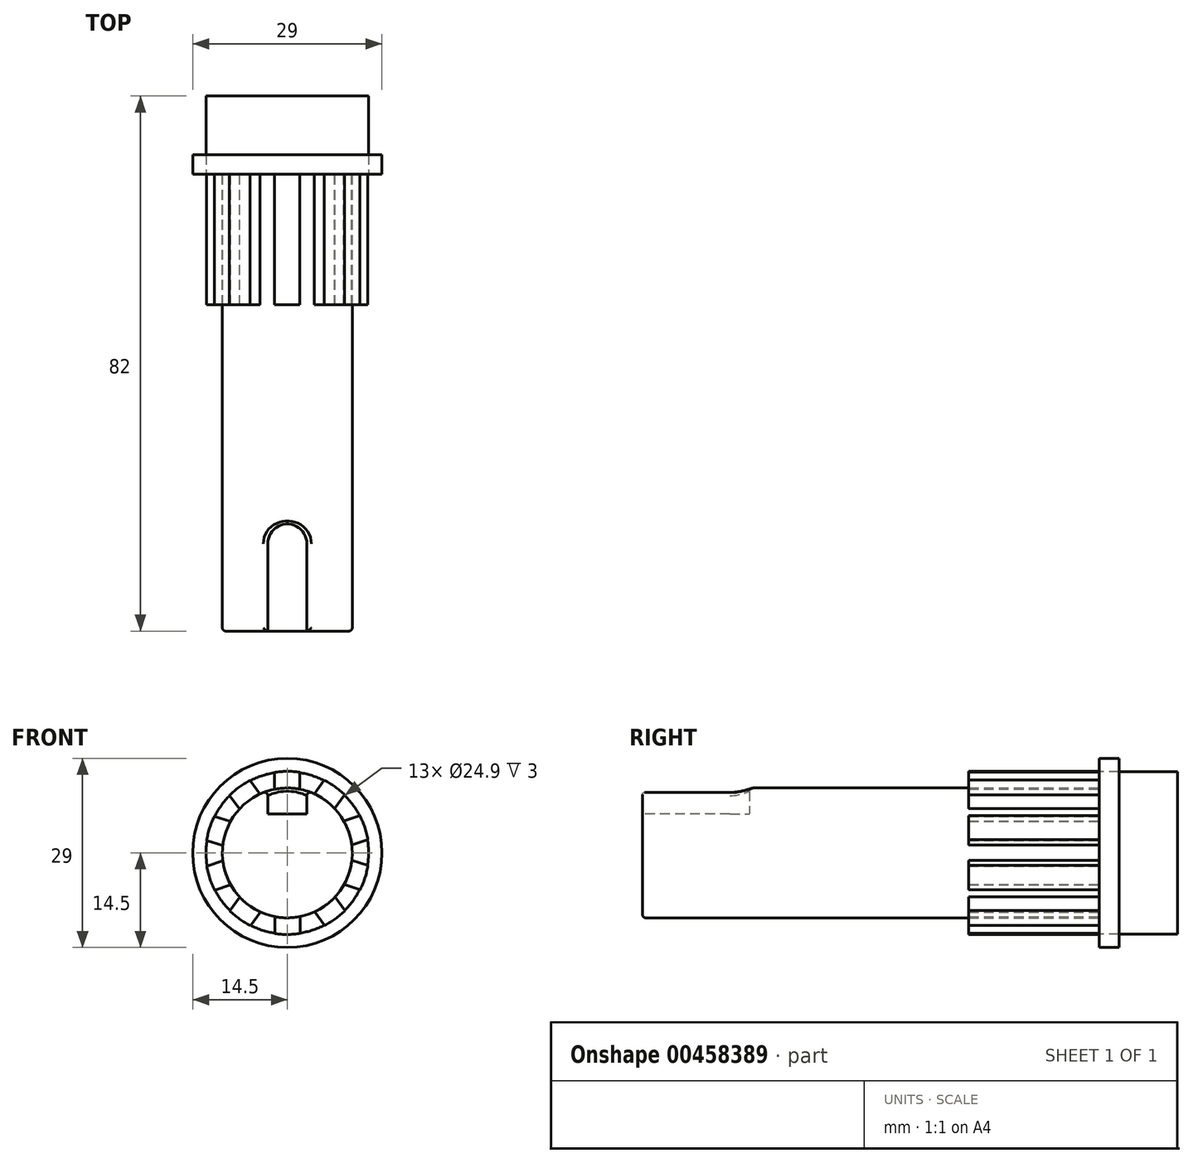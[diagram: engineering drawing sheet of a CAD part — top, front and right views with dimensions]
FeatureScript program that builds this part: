
annotation { "Feature Type Name" : "Feature", "Feature Type Description" : "" }
export const myFeature = defineFeature(function(context is Context, id is Id, definition is map)
    precondition{}
    {
        {
            var Q0;
            Q0=qCreatedBy(makeId("Front.planeOp"),FACE);
            var sketch = newSketch(context, id + "F0", { "sketchPlane" : qUnion([Q0])});
            skCircle(sketch, "E0", {"center": v(0, 0) * mm, "radius": 14.5 * mm});
            skCircle(sketch, "E1", {"center": v(0, 0) * mm, "radius": 9.95 * mm});
            skArc(sketch, "E2", {"start": v(-1.9, -12.36) * mm, "mid": v(0.05, -12.5) * mm, "end": v(1.99, -12.34) * mm});
            skLineSegment(sketch, "E3", {"start": v(-1.9, -12.36) * mm, "end": v(-1.9, -9.77) * mm});
            skLineSegment(sketch, "E4", {"start": v(1.97, -9.75) * mm, "end": v(1.99, -12.34) * mm});
            skLineSegment(sketch, "E5.1.0", {"start": v(7.32, -6.73) * mm, "end": v(8.86, -8.81) * mm});
            skLineSegment(sketch, "E5.1.2", {"start": v(5.73, -11.1) * mm, "end": v(4.2, -9.02) * mm});
            skArc(sketch, "E5.1.3", {"start": v(5.73, -11.1) * mm, "mid": v(7.39, -10.08) * mm, "end": v(8.86, -8.81) * mm});
            skLineSegment(sketch, "E5.2.0", {"start": v(9.88, -1.14) * mm, "end": v(12.35, -1.92) * mm});
            skLineSegment(sketch, "E5.2.2", {"start": v(11.17, -5.62) * mm, "end": v(8.7, -4.82) * mm});
            skArc(sketch, "E5.2.3", {"start": v(11.17, -5.62) * mm, "mid": v(11.9, -3.82) * mm, "end": v(12.35, -1.92) * mm});
            skLineSegment(sketch, "E5.3.0", {"start": v(8.67, 4.88) * mm, "end": v(11.12, 5.7) * mm});
            skLineSegment(sketch, "E5.3.2", {"start": v(12.34, 2.02) * mm, "end": v(9.88, 1.22) * mm});
            skArc(sketch, "E5.3.3", {"start": v(12.34, 2.02) * mm, "mid": v(11.87, 3.9) * mm, "end": v(11.12, 5.7) * mm});
            skLineSegment(sketch, "E5.4.0", {"start": v(4.14, 9.05) * mm, "end": v(5.64, 11.15) * mm});
            skLineSegment(sketch, "E5.4.2", {"start": v(8.8, 8.88) * mm, "end": v(7.27, 6.79) * mm});
            skArc(sketch, "E5.4.3", {"start": v(8.8, 8.88) * mm, "mid": v(7.3, 10.14) * mm, "end": v(5.64, 11.15) * mm});
            skLineSegment(sketch, "E5.5.0", {"start": v(-1.97, 9.75) * mm, "end": v(-1.99, 12.34) * mm});
            skLineSegment(sketch, "E5.5.2", {"start": v(1.9, 12.36) * mm, "end": v(1.9, 9.77) * mm});
            skArc(sketch, "E5.5.3", {"start": v(1.9, 12.36) * mm, "mid": v(-0.05, 12.5) * mm, "end": v(-1.99, 12.34) * mm});
            skLineSegment(sketch, "E5.6.0", {"start": v(-7.32, 6.73) * mm, "end": v(-8.86, 8.81) * mm});
            skLineSegment(sketch, "E5.6.2", {"start": v(-5.73, 11.1) * mm, "end": v(-4.2, 9.02) * mm});
            skArc(sketch, "E5.6.3", {"start": v(-5.73, 11.1) * mm, "mid": v(-7.39, 10.08) * mm, "end": v(-8.86, 8.81) * mm});
            skLineSegment(sketch, "E5.7.0", {"start": v(-9.88, 1.14) * mm, "end": v(-12.35, 1.92) * mm});
            skLineSegment(sketch, "E5.7.2", {"start": v(-11.17, 5.62) * mm, "end": v(-8.7, 4.82) * mm});
            skArc(sketch, "E5.7.3", {"start": v(-11.17, 5.62) * mm, "mid": v(-11.9, 3.82) * mm, "end": v(-12.35, 1.92) * mm});
            skLineSegment(sketch, "E5.8.0", {"start": v(-8.67, -4.88) * mm, "end": v(-11.12, -5.7) * mm});
            skLineSegment(sketch, "E5.8.2", {"start": v(-12.34, -2.02) * mm, "end": v(-9.88, -1.22) * mm});
            skArc(sketch, "E5.8.3", {"start": v(-12.34, -2.02) * mm, "mid": v(-11.87, -3.9) * mm, "end": v(-11.12, -5.7) * mm});
            skLineSegment(sketch, "E5.9.0", {"start": v(-4.14, -9.05) * mm, "end": v(-5.64, -11.15) * mm});
            skLineSegment(sketch, "E5.9.2", {"start": v(-8.8, -8.88) * mm, "end": v(-7.27, -6.79) * mm});
            skArc(sketch, "E5.9.3", {"start": v(-8.8, -8.88) * mm, "mid": v(-7.3, -10.14) * mm, "end": v(-5.64, -11.15) * mm});
            skSolve(sketch);
        }
        {
            var Q0;
            Q0=qCreatedBy(makeId("Front.planeOp"),FACE);
            var sketch = newSketch(context, id + "F1", { "sketchPlane" : qUnion([Q0])});
            skCircle(sketch, "E6", {"center": v(0, 0) * mm, "radius": 12.45 * mm});
            skCircle(sketch, "E7", {"center": v(0, 0) * mm, "radius": 14.5 * mm});
            skSolve(sketch);
        }
        {
            var Q0;
            Q0 = qSketchRegion(id + "F1", true);
            extrude(context, id + "F2", {"entities" : qUnion([Q0]), "oppositeDirection" : true, "depth" : 3 * mm});
        }
        {
            var Q0;
            Q0=makeQuery(id+"F1.imprint","IMPRINT",FACE,{"disambiguationData":[TD([[makeQuery(id+"F1.imprint","IMPRINT",EDGE,{"derivedFrom":sQuery(id+"F1.wireOp",EDGE,"E6")}),1.0]])]});
            var Q1;
            Q1=sQuery(id+"F1.wireOp",EDGE,"E6");
            extrude(context, id + "F3", {"entities" : qUnion([Q0]), "surfaceEntities" : qUnion([Q1]), "oppositeDirection" : true, "depth" : 12 * mm});
        }
        {
            var Q0;
            {var subQ5=sQuery(id+"F0.wireOp",EDGE,"E5.6.3");Q0=makeQuery(id+"F0.imprint","IMPRINT",FACE,{"disambiguationData":[TD([[makeQuery(id+"F0.imprint","IMPRINT",EDGE,{"derivedFrom":subQ5}),1.0]])]});}
            var Q1;
            {var subQ5=sQuery(id+"F0.wireOp",EDGE,"E5.5.3");Q1=makeQuery(id+"F0.imprint","IMPRINT",FACE,{"disambiguationData":[TD([[makeQuery(id+"F0.imprint","IMPRINT",EDGE,{"derivedFrom":subQ5}),1.0]])]});}
            var Q2;
            {var subQ5=sQuery(id+"F0.wireOp",EDGE,"E5.4.3");Q2=makeQuery(id+"F0.imprint","IMPRINT",FACE,{"disambiguationData":[TD([[makeQuery(id+"F0.imprint","IMPRINT",EDGE,{"derivedFrom":subQ5}),1.0]])]});}
            var Q3;
            {var subQ5=sQuery(id+"F0.wireOp",EDGE,"E5.3.3");Q3=makeQuery(id+"F0.imprint","IMPRINT",FACE,{"disambiguationData":[TD([[makeQuery(id+"F0.imprint","IMPRINT",EDGE,{"derivedFrom":subQ5}),1.0]])]});}
            var Q4;
            {var subQ5=sQuery(id+"F0.wireOp",EDGE,"E5.2.3");Q4=makeQuery(id+"F0.imprint","IMPRINT",FACE,{"disambiguationData":[TD([[makeQuery(id+"F0.imprint","IMPRINT",EDGE,{"derivedFrom":subQ5}),1.0]])]});}
            var Q5;
            {var subQ5=sQuery(id+"F0.wireOp",EDGE,"E5.1.3");Q5=makeQuery(id+"F0.imprint","IMPRINT",FACE,{"disambiguationData":[TD([[makeQuery(id+"F0.imprint","IMPRINT",EDGE,{"derivedFrom":subQ5}),1.0]])]});}
            var Q6;
            {var subQ5=sQuery(id+"F0.wireOp",EDGE,"E2");Q6=makeQuery(id+"F0.imprint","IMPRINT",FACE,{"disambiguationData":[TD([[makeQuery(id+"F0.imprint","IMPRINT",EDGE,{"derivedFrom":subQ5}),1.0]])]});}
            var Q7;
            {var subQ5=sQuery(id+"F0.wireOp",EDGE,"E5.9.3");Q7=makeQuery(id+"F0.imprint","IMPRINT",FACE,{"disambiguationData":[TD([[makeQuery(id+"F0.imprint","IMPRINT",EDGE,{"derivedFrom":subQ5}),1.0]])]});}
            var Q8;
            {var subQ5=sQuery(id+"F0.wireOp",EDGE,"E5.8.3");Q8=makeQuery(id+"F0.imprint","IMPRINT",FACE,{"disambiguationData":[TD([[makeQuery(id+"F0.imprint","IMPRINT",EDGE,{"derivedFrom":subQ5}),1.0]])]});}
            var Q9;
            {var subQ5=sQuery(id+"F0.wireOp",EDGE,"E5.7.3");Q9=makeQuery(id+"F0.imprint","IMPRINT",FACE,{"disambiguationData":[TD([[makeQuery(id+"F0.imprint","IMPRINT",EDGE,{"derivedFrom":subQ5}),1.0]])]});}
            extrude(context, id + "F4", {"entities" : qUnion([Q0, Q1, Q2, Q3, Q4, Q5, Q6, Q7, Q8, Q9]), "depth" : 20 * mm});
        }
        {
            var Q0;
            {var subQ0=sQuery(id+"F0.wireOp",EDGE,"E1");var subQ8=makeQuery(id+"F0.imprint","INTERSECT",VERTEX,{"derivedFrom":[sQuery(id+"F0.wireOp",EDGE,"E5.3.0"),subQ0]});Q0=makeQuery(id+"F0.imprint","IMPRINT",FACE,{"disambiguationData":[TD([[makeQuery(id+"F0.imprint","IMPRINT",EDGE,{"disambiguationData":[TD([[subQ8,1.0]])],"derivedFrom":subQ0}),1.0]])]});}
            var Q1;
            Q1=sQuery(id+"F0.wireOp",EDGE,"E1");
            extrude(context, id + "F5", {"entities" : qUnion([Q0]), "surfaceEntities" : qUnion([Q1]), "depth" : 70 * mm});
        }
        {
            var Q0;
            Q0=qCreatedBy(makeId("Top.planeOp"),FACE);
            cPlane(context, id + "F6", {"entities" : qUnion([Q0]), "cplaneType" : CPlaneType.OFFSET, "offset" : 6 * mm, "width" : 150 * mm, "height" : 150 * mm});
        }
        {
            var Q0;
            Q0=qCreatedBy(id+"F6.planeOp",FACE);
            var sketch = newSketch(context, id + "F7", { "sketchPlane" : qUnion([Q0])});
            skLineSegment(sketch, "E8.bottom", {"start": v(0, -74.6) * mm, "end": v(-3, -74.6) * mm});
            skLineSegment(sketch, "E8.right", {"start": v(-3, -74.6) * mm, "end": v(-3, -56.6) * mm});
            skLineSegment(sketch, "E9.top", {"start": v(0, -74.6) * mm, "end": v(3, -74.6) * mm});
            skLineSegment(sketch, "E9.right", {"start": v(3, -56.6) * mm, "end": v(3, -74.6) * mm});
            skArc(sketch, "E10", {"start": v(3, -56.6) * mm, "mid": v(0, -53.6) * mm, "end": v(-3, -56.6) * mm});
            skSolve(sketch);
        }
        {
            var Q0;
            Q0 = qSketchRegion(id + "F7", true);
            extrude(context, id + "F8", {"entities" : qUnion([Q0]), "operationType" : NewBodyOperationType.REMOVE, "depth" : 25 * mm});
        }
        {
            var Q0;
            Q0=makeQuery(id+"F8.boolean.opBoolean","INTERSECT",EDGE,{"derivedFrom":[makeQuery(id+"F5.opExtrude","SWEPT_FACE",FACE,{"disambiguationData":[OSD([sQuery(id+"F0.wireOp",EDGE,"E1")])]}),makeQuery(id+"F8.opExtrude","SWEPT_FACE",FACE,{"disambiguationData":[OSD([sQuery(id+"F7.wireOp",EDGE,"E8.right")])]})]});
            var Q1;
            Q1=makeQuery(id+"F8.boolean.opBoolean","INTERSECT",EDGE,{"derivedFrom":[makeQuery(id+"F5.opExtrude","SWEPT_FACE",FACE,{"disambiguationData":[OSD([sQuery(id+"F0.wireOp",EDGE,"E1")])]}),makeQuery(id+"F8.opExtrude","SWEPT_FACE",FACE,{"disambiguationData":[OSD([sQuery(id+"F7.wireOp",EDGE,"E10")])]})]});
            var Q2;
            Q2=makeQuery(id+"F8.boolean.opBoolean","INTERSECT",EDGE,{"derivedFrom":[makeQuery(id+"F5.opExtrude","SWEPT_FACE",FACE,{"disambiguationData":[OSD([sQuery(id+"F0.wireOp",EDGE,"E1")])]}),makeQuery(id+"F8.opExtrude","SWEPT_FACE",FACE,{"disambiguationData":[OSD([sQuery(id+"F7.wireOp",EDGE,"E9.right")])]})]});
            var Q3;
            Q3=makeQuery(id+"F5.opExtrude","CAP_EDGE",EDGE,{"disambiguationData":[OSD([sQuery(id+"F0.wireOp",EDGE,"E1")])],"isStart":false});
            fillet(context, id + "F9", {"entities" : qUnion([Q0, Q1, Q2, Q3]), "radius" : 0.5 * mm, "tangentPropagation" : true, "allowEdgeOverflow" : false});
        }
    });
